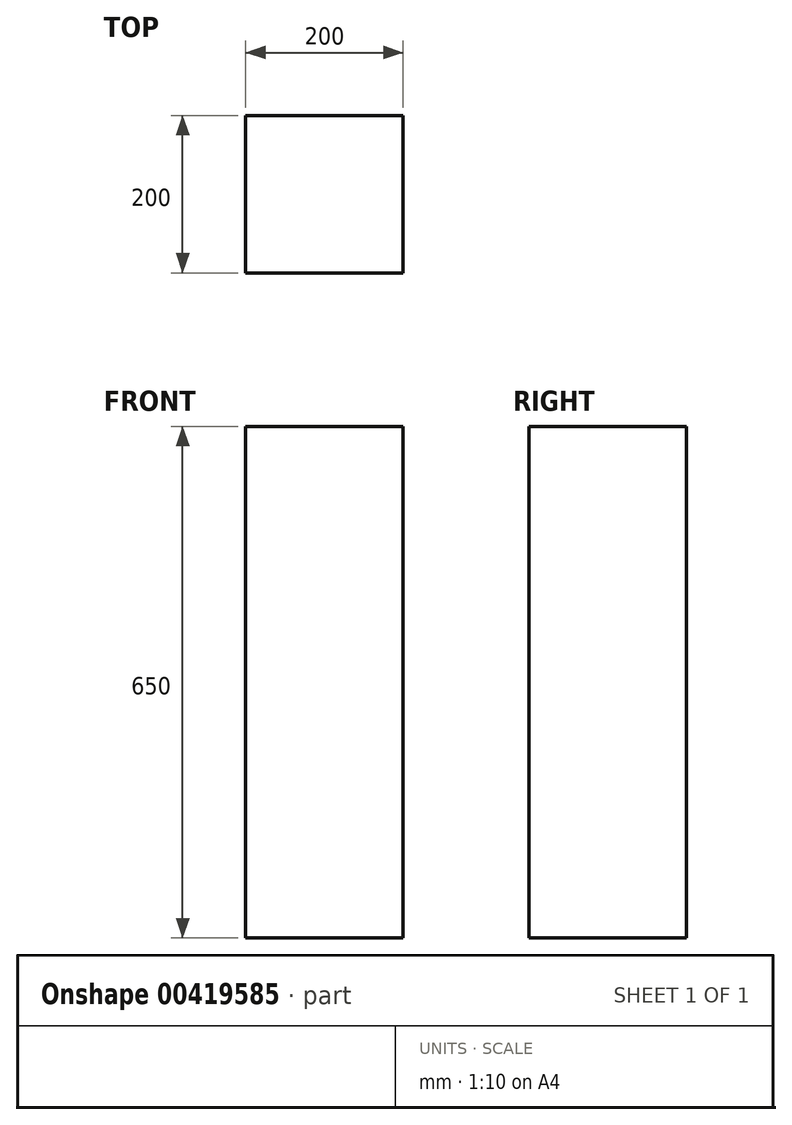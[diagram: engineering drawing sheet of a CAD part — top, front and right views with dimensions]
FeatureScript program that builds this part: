
annotation { "Feature Type Name" : "Feature", "Feature Type Description" : "" }
export const myFeature = defineFeature(function(context is Context, id is Id, definition is map)
    precondition{}
    {
        {
            var Q0;
            Q0=qCreatedBy(makeId("Top.planeOp"),FACE);
            var sketch = newSketch(context, id + "F0", { "sketchPlane" : qUnion([Q0])});
            skLineSegment(sketch, "E0.bottom", {"start": v(-112.62, 134.32) * mm, "end": v(87.38, 134.32) * mm});
            skLineSegment(sketch, "E0.top", {"start": v(-112.62, -65.68) * mm, "end": v(87.38, -65.68) * mm});
            skLineSegment(sketch, "E0.left", {"start": v(-112.62, 134.32) * mm, "end": v(-112.62, -65.68) * mm});
            skLineSegment(sketch, "E0.right", {"start": v(87.38, 134.32) * mm, "end": v(87.38, -65.68) * mm});
            skSolve(sketch);
        }
        {
            var Q0;
            Q0=makeQuery(id+"F0.imprint","IMPRINT",FACE,{"disambiguationData":[TD([[makeQuery(id+"F0.imprint","IMPRINT",EDGE,{"derivedFrom":sQuery(id+"F0.wireOp",EDGE,"E0.bottom")}),-1.0]])]});
            extrude(context, id + "F1", {"entities" : qUnion([Q0]), "depth" : 650 * mm});
        }
    });
